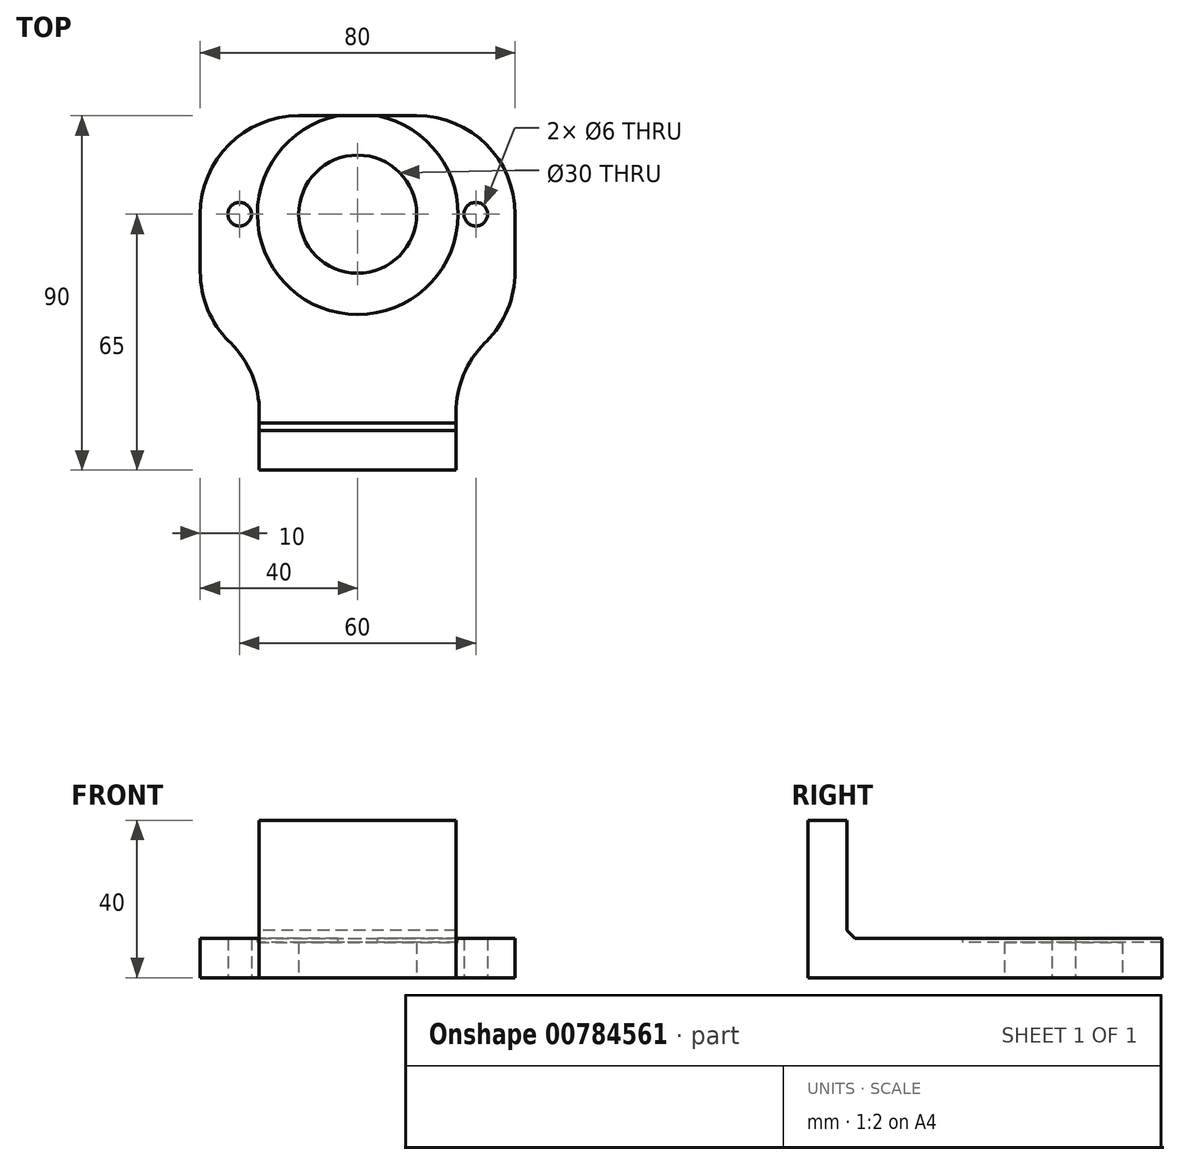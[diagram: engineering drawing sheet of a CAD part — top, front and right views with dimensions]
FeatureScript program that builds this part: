
annotation { "Feature Type Name" : "Feature", "Feature Type Description" : "" }
export const myFeature = defineFeature(function(context is Context, id is Id, definition is map)
    precondition{}
    {
        {
            var Q0;
            Q0=qCreatedBy(makeId("Top.planeOp"),FACE);
            var sketch = newSketch(context, id + "F0", { "sketchPlane" : qUnion([Q0])});
            skCircle(sketch, "E0", {"center": v(0, 0) * mm, "radius": 15 * mm});
            skLineSegment(sketch, "E1.bottom", {"start": v(40, 25) * mm, "end": v(-40, 25) * mm});
            skLineSegment(sketch, "E1.top", {"start": v(40, -25) * mm, "end": v(-40, -25) * mm});
            skLineSegment(sketch, "E1.left", {"start": v(40, 25) * mm, "end": v(40, -25) * mm});
            skLineSegment(sketch, "E1.right", {"start": v(-40, 25) * mm, "end": v(-40, -25) * mm});
            skLineSegment(sketch, "E2", {"start": v(0, 0) * mm, "end": v(0, -65) * mm, "construction": true});
            skLineSegment(sketch, "E3", {"start": v(-25, -25) * mm, "end": v(-25, -65) * mm});
            skLineSegment(sketch, "E4", {"start": v(-25, -65) * mm, "end": v(25, -65) * mm});
            skLineSegment(sketch, "E5", {"start": v(25, -65) * mm, "end": v(25, -25) * mm});
            skLineSegment(sketch, "E6", {"start": v(0, 0) * mm, "end": v(30, 0) * mm, "construction": true});
            skCircle(sketch, "E7", {"center": v(30, 0) * mm, "radius": 3 * mm});
            skLineSegment(sketch, "E8", {"start": v(0, 0) * mm, "end": v(-30, 0) * mm, "construction": true});
            skCircle(sketch, "E9", {"center": v(-30, 0) * mm, "radius": 3 * mm});
            skLineSegment(sketch, "E10", {"start": v(-25, -55) * mm, "end": v(25, -55) * mm});
            skSolve(sketch);
        }
        {
            var Q0;
            {var subQ0=sQuery(id+"F0.wireOp",EDGE,"E3");Q0=makeQuery(id+"F0.imprint","IMPRINT",FACE,{"disambiguationData":[TD([[makeQuery(id+"F0.imprint","IMPRINT",EDGE,{"derivedFrom":subQ0}),1.0]])]});}
            var Q1;
            Q1=makeQuery(id+"F0.imprint","IMPRINT",FACE,{"disambiguationData":[TD([[makeQuery(id+"F0.imprint","IMPRINT",EDGE,{"derivedFrom":sQuery(id+"F0.wireOp",EDGE,"E0")}),-1.0]])]});
            extrude(context, id + "F1", {"entities" : qUnion([Q0, Q1]), "depth" : 10 * mm, "offsetDistance" : 25 * mm});
        }
        {
            var Q0;
            {var subQ0=sQuery(id+"F0.wireOp",EDGE,"E4");Q0=makeQuery(id+"F0.imprint","IMPRINT",FACE,{"disambiguationData":[TD([[makeQuery(id+"F0.imprint","IMPRINT",EDGE,{"derivedFrom":subQ0}),1.0]])]});}
            extrude(context, id + "F2", {"entities" : qUnion([Q0]), "operationType" : NewBodyOperationType.ADD, "depth" : 40 * mm, "offsetDistance" : 25 * mm});
        }
        {
            var Q0;
            Q0=makeQuery(id+"F1.opExtrude","SWEPT_EDGE",EDGE,{"disambiguationData":[OSD([sQuery(id+"F0.wireOp",EDGE,"E1.top"),sQuery(id+"F0.wireOp",EDGE,"E5")])]});
            var Q1;
            Q1=makeQuery(id+"F1.opExtrude","SWEPT_EDGE",EDGE,{"disambiguationData":[OSD([sQuery(id+"F0.wireOp",EDGE,"E1.top"),sQuery(id+"F0.wireOp",EDGE,"E3")])]});
            chamfer(context, id + "F3", {"entities" : qUnion([Q0, Q1]), "width" : 15 * mm, "tangentPropagation" : true});
        }
        {
            var Q0;
            Q0=makeQuery(id+"F3.opChamfer","BLEND_EDGE",EDGE,{"blendedFrom":[makeQuery(id+"F1.opExtrude","SWEPT_EDGE",EDGE,{"disambiguationData":[OSD([sQuery(id+"F0.wireOp",EDGE,"E1.top"),sQuery(id+"F0.wireOp",EDGE,"E5")])]}),makeQuery(id+"F1.opExtrude","SWEPT_FACE",FACE,{"disambiguationData":[OSD([sQuery(id+"F0.wireOp",EDGE,"E1.left")])]})],"blendedInto":[makeQuery(id+"F1.opExtrude","SWEPT_FACE",FACE,{"disambiguationData":[OSD([sQuery(id+"F0.wireOp",EDGE,"E1.left")])]})]});
            var Q1;
            {var subQ0=sQuery(id+"F0.wireOp",EDGE,"E5");Q1=makeQuery(id+"F3.opChamfer","BLEND_EDGE",EDGE,{"blendedFrom":[makeQuery(id+"F1.opExtrude","SWEPT_EDGE",EDGE,{"disambiguationData":[OSD([sQuery(id+"F0.wireOp",EDGE,"E1.top"),subQ0])]}),makeQuery(id+"F2.boolean.opBoolean","MERGE",FACE,{"derivedFrom":[makeQuery(id+"F1.opExtrude","SWEPT_FACE",FACE,{"disambiguationData":[OSD([subQ0])]}),makeQuery(id+"F2.opExtrude","SWEPT_FACE",FACE,{"disambiguationData":[OSD([subQ0])]})]})],"blendedInto":[makeQuery(id+"F2.boolean.opBoolean","MERGE",FACE,{"derivedFrom":[makeQuery(id+"F1.opExtrude","SWEPT_FACE",FACE,{"disambiguationData":[OSD([subQ0])]}),makeQuery(id+"F2.opExtrude","SWEPT_FACE",FACE,{"disambiguationData":[OSD([subQ0])]})]})]});}
            var Q2;
            Q2=makeQuery(id+"F1.opExtrude","SWEPT_EDGE",EDGE,{"disambiguationData":[OSD([sQuery(id+"F0.wireOp",EDGE,"E1.bottom"),sQuery(id+"F0.wireOp",EDGE,"E1.left")])]});
            var Q3;
            {var subQ0=sQuery(id+"F0.wireOp",EDGE,"E3");Q3=makeQuery(id+"F3.opChamfer","BLEND_EDGE",EDGE,{"blendedFrom":[makeQuery(id+"F1.opExtrude","SWEPT_EDGE",EDGE,{"disambiguationData":[OSD([sQuery(id+"F0.wireOp",EDGE,"E1.top"),subQ0])]}),makeQuery(id+"F2.boolean.opBoolean","MERGE",FACE,{"derivedFrom":[makeQuery(id+"F1.opExtrude","SWEPT_FACE",FACE,{"disambiguationData":[OSD([subQ0])]}),makeQuery(id+"F2.opExtrude","SWEPT_FACE",FACE,{"disambiguationData":[OSD([subQ0])]})]})],"blendedInto":[makeQuery(id+"F2.boolean.opBoolean","MERGE",FACE,{"derivedFrom":[makeQuery(id+"F1.opExtrude","SWEPT_FACE",FACE,{"disambiguationData":[OSD([subQ0])]}),makeQuery(id+"F2.opExtrude","SWEPT_FACE",FACE,{"disambiguationData":[OSD([subQ0])]})]})]});}
            var Q4;
            Q4=makeQuery(id+"F3.opChamfer","BLEND_EDGE",EDGE,{"blendedFrom":[makeQuery(id+"F1.opExtrude","SWEPT_EDGE",EDGE,{"disambiguationData":[OSD([sQuery(id+"F0.wireOp",EDGE,"E1.top"),sQuery(id+"F0.wireOp",EDGE,"E3")])]}),makeQuery(id+"F1.opExtrude","SWEPT_FACE",FACE,{"disambiguationData":[OSD([sQuery(id+"F0.wireOp",EDGE,"E1.right")])]})],"blendedInto":[makeQuery(id+"F1.opExtrude","SWEPT_FACE",FACE,{"disambiguationData":[OSD([sQuery(id+"F0.wireOp",EDGE,"E1.right")])]})]});
            var Q5;
            Q5=makeQuery(id+"F1.opExtrude","SWEPT_EDGE",EDGE,{"disambiguationData":[OSD([sQuery(id+"F0.wireOp",EDGE,"E1.bottom"),sQuery(id+"F0.wireOp",EDGE,"E1.right")])]});
            fillet(context, id + "F4", {"entities" : qUnion([Q0, Q1, Q2, Q3, Q4, Q5]), "radius" : 25 * mm, "tangentPropagation" : true, "allowEdgeOverflow" : false});
        }
        {
            var Q0;
            Q0=makeQuery(id+"F2.boolean.opBoolean","INTERSECT",EDGE,{"derivedFrom":[makeQuery(id+"F1.opExtrude","CAP_FACE",FACE,{"disambiguationData":[OSD([sQuery(id+"F0.wireOp",EDGE,"E0"),sQuery(id+"F0.wireOp",EDGE,"E1.bottom"),sQuery(id+"F0.wireOp",EDGE,"E1.top"),sQuery(id+"F0.wireOp",EDGE,"E1.left"),sQuery(id+"F0.wireOp",EDGE,"E1.right"),sQuery(id+"F0.wireOp",EDGE,"E3"),sQuery(id+"F0.wireOp",EDGE,"E4"),sQuery(id+"F0.wireOp",EDGE,"E5"),sQuery(id+"F0.wireOp",EDGE,"E7"),sQuery(id+"F0.wireOp",EDGE,"E9")])],"isStart":false}),makeQuery(id+"F2.opExtrude","SWEPT_FACE",FACE,{"disambiguationData":[OSD([sQuery(id+"F0.wireOp",EDGE,"E10")])]})]});
            chamfer(context, id + "F5", {"entities" : qUnion([Q0]), "width" : 2 * mm, "tangentPropagation" : true});
        }
        {
            var Q0;
            Q0=makeQuery(id+"F1.opExtrude","CAP_FACE",FACE,{"disambiguationData":[OSD([sQuery(id+"F0.wireOp",EDGE,"E0"),sQuery(id+"F0.wireOp",EDGE,"E1.bottom"),sQuery(id+"F0.wireOp",EDGE,"E1.top"),sQuery(id+"F0.wireOp",EDGE,"E1.left"),sQuery(id+"F0.wireOp",EDGE,"E1.right"),sQuery(id+"F0.wireOp",EDGE,"E3"),sQuery(id+"F0.wireOp",EDGE,"E4"),sQuery(id+"F0.wireOp",EDGE,"E5"),sQuery(id+"F0.wireOp",EDGE,"E7"),sQuery(id+"F0.wireOp",EDGE,"E9")])],"isStart":false});
            var sketch = newSketch(context, id + "F6", { "sketchPlane" : qUnion([Q0])});
            skCircle(sketch, "E11", {"center": v(0, 0) * mm, "radius": 25.5 * mm});
            skSolve(sketch);
        }
        {
            var Q0;
            Q0 = qSketchRegion(id + "F6", true);
            extrude(context, id + "F7", {"entities" : qUnion([Q0]), "operationType" : NewBodyOperationType.REMOVE, "oppositeDirection" : true, "depth" : 1 * mm, "offsetDistance" : 25 * mm});
        }
    });
